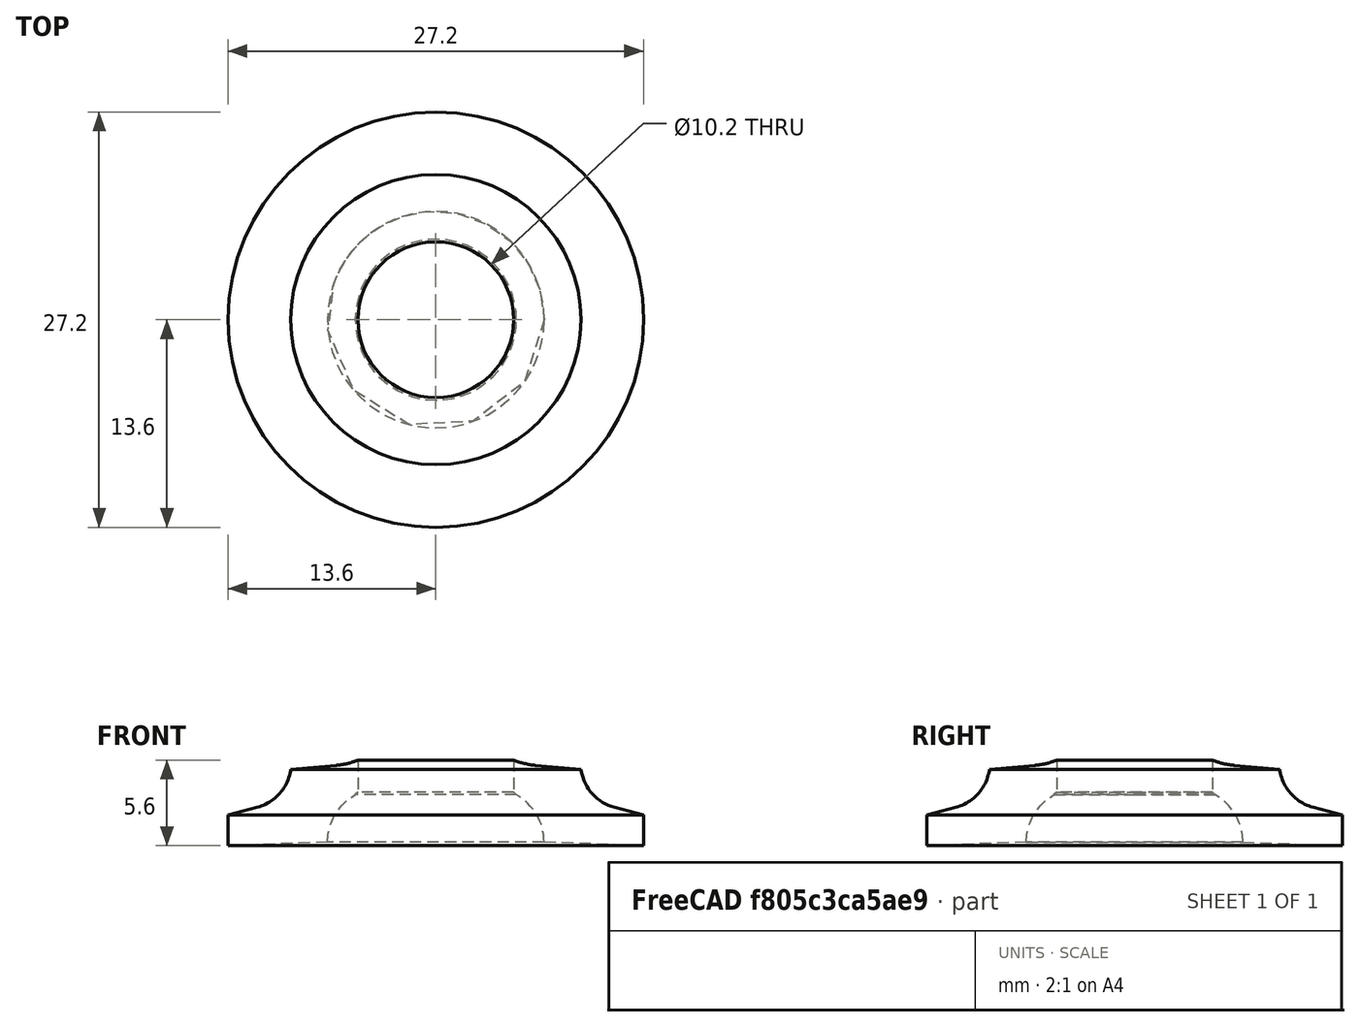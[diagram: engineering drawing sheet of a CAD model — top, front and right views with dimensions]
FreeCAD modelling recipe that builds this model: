
FCSTD DOCUMENT  (FreeCAD 0.19R22894 (Git))
Label: bear head screw
License: All rights reserved
LicenseURL: http://en.wikipedia.org/wiki/All_rights_reserved
objects: App::Part×1, Sketcher::SketchObject×1, Part::Revolution×1
note: 2 computed .brp shape members not serialized (recipe doc carries the construction recipe); baked Part::Feature solids carry a one-line shape summary decoded from their .brp

FEATURE [App::Part] Part
  Origin = -> Origin
FEATURE [Sketcher::SketchObject] Sketch
  Placement = pos=(0,0,0) rot=(-1,0,0;4.71239rad)
  sketch-geometry (13):
    g0: LineSegment StartX=5.1 StartY=5.6 StartZ=0 EndX=5.1 EndY=3.5 EndZ=0
    g1: LineSegment StartX=13.6 StartY=2 StartZ=0 EndX=13.6 EndY=0 EndZ=0
    g2: LineSegment StartX=5.27114 StartY=3.32886 StartZ=0 EndX=5.1 EndY=3.5 EndZ=0
    g3: LineSegment [constr] StartX=0 StartY=21.8379 StartZ=0 EndX=0 EndY=-4.77387 EndZ=0
    g4: LineSegment StartX=9.5 StartY=5 StartZ=0 EndX=6.52372 EndY=5.26039 EndZ=0
    g5: ArcOfCircle CenterX=6.9595 CenterY=10.2414 CenterZ=0 NormalX=0 NormalY=0 NormalZ=1 AngleXU=0 Radius=5 StartAngle=4.33133 EndAngle=4.62512
    g6: LineSegment [constr] StartX=13.6 StartY=2 StartZ=0 EndX=18.0882 EndY=2 EndZ=0
    g7: LineSegment StartX=9.5 StartY=5 StartZ=0 EndX=9.52002 EndY=4.88647 EndZ=0
    g8: LineSegment StartX=13.6 StartY=2 StartZ=0 EndX=11.698 EndY=2.50964 EndZ=0
    g9: ArcOfCircle CenterX=12.4744 CenterY=5.40742 CenterZ=0 NormalX=0 NormalY=0 NormalZ=1 AngleXU=0 Radius=3 StartAngle=3.31613 EndAngle=4.45059
    g10: LineSegment StartX=13.6 StartY=0 StartZ=0 EndX=7.08988 EndY=0.227339 EndZ=0
    g11: LineSegment [constr] StartX=7.08988 StartY=0.227339 StartZ=0 EndX=7.08988 EndY=2.72666 EndZ=0
    g12: ArcOfCircle CenterX=3.53597 CenterY=0.227339 CenterZ=0 NormalX=0 NormalY=0 NormalZ=1 AngleXU=0 Radius=3.5539 StartAngle=6.28319 EndAngle=7.34391
  constraints (35):
    c: Vertical(g0)
    c: PointOnObject(g1,g-1)
    c: Coincident(g2,g0)
    c: DistanceY(g0,g0) = 2.1
    c: Vertical(g1)
    c: Angle(g2,g-1) = 0.785398
    c: PointOnObject(g3,g-2)
    c: PointOnObject(g3,g-2)
    c: DistanceX(g-1,g0) = 5.1
    c: DistanceY(g1,g1) = 2
    c: Coincident(g5,g4)
    c: Coincident(g5,g0)
    c: Tangent(g4,g5)
    c: Angle(g4,g-1) = 0.0872665
    c: DistanceY(g1,g4) = 5
    c: DistanceX(g-1,g1) = 13.6
    c: DistanceX(g-1,g4) = 9.5
    c: Coincident(g6,g1)
    c: Horizontal(g6)
    c: Coincident(g7,g4)
    c: Coincident(g8,g1)
    c: Coincident(g9,g7)
    c: Coincident(g9,g8)
    c: Tangent(g8,g9)
    c: Tangent(g7,g9)
    c: Radius(g9) = 3
    c: Radius(g5) = 5
    c: Angle(g3,g7) = 0.174533
    c: Coincident(g10,g1)
    c: Coincident(g11,g10)
    c: Vertical(g11)
    c: Coincident(g12,g2)
    c: Coincident(g12,g10)
    c: Tangent(g12,g11)
    c: Angle(g10,g-1) = 0.0349066
FEATURE [Part::Revolution] Revolve
  Angle = 360
  Axis = (0,0,1)
  Base = (0,0,0)
  FaceMakerClass = Part::FaceMakerBullseye
  Solid = true
  Source = -> Sketch
  Symmetric = false
